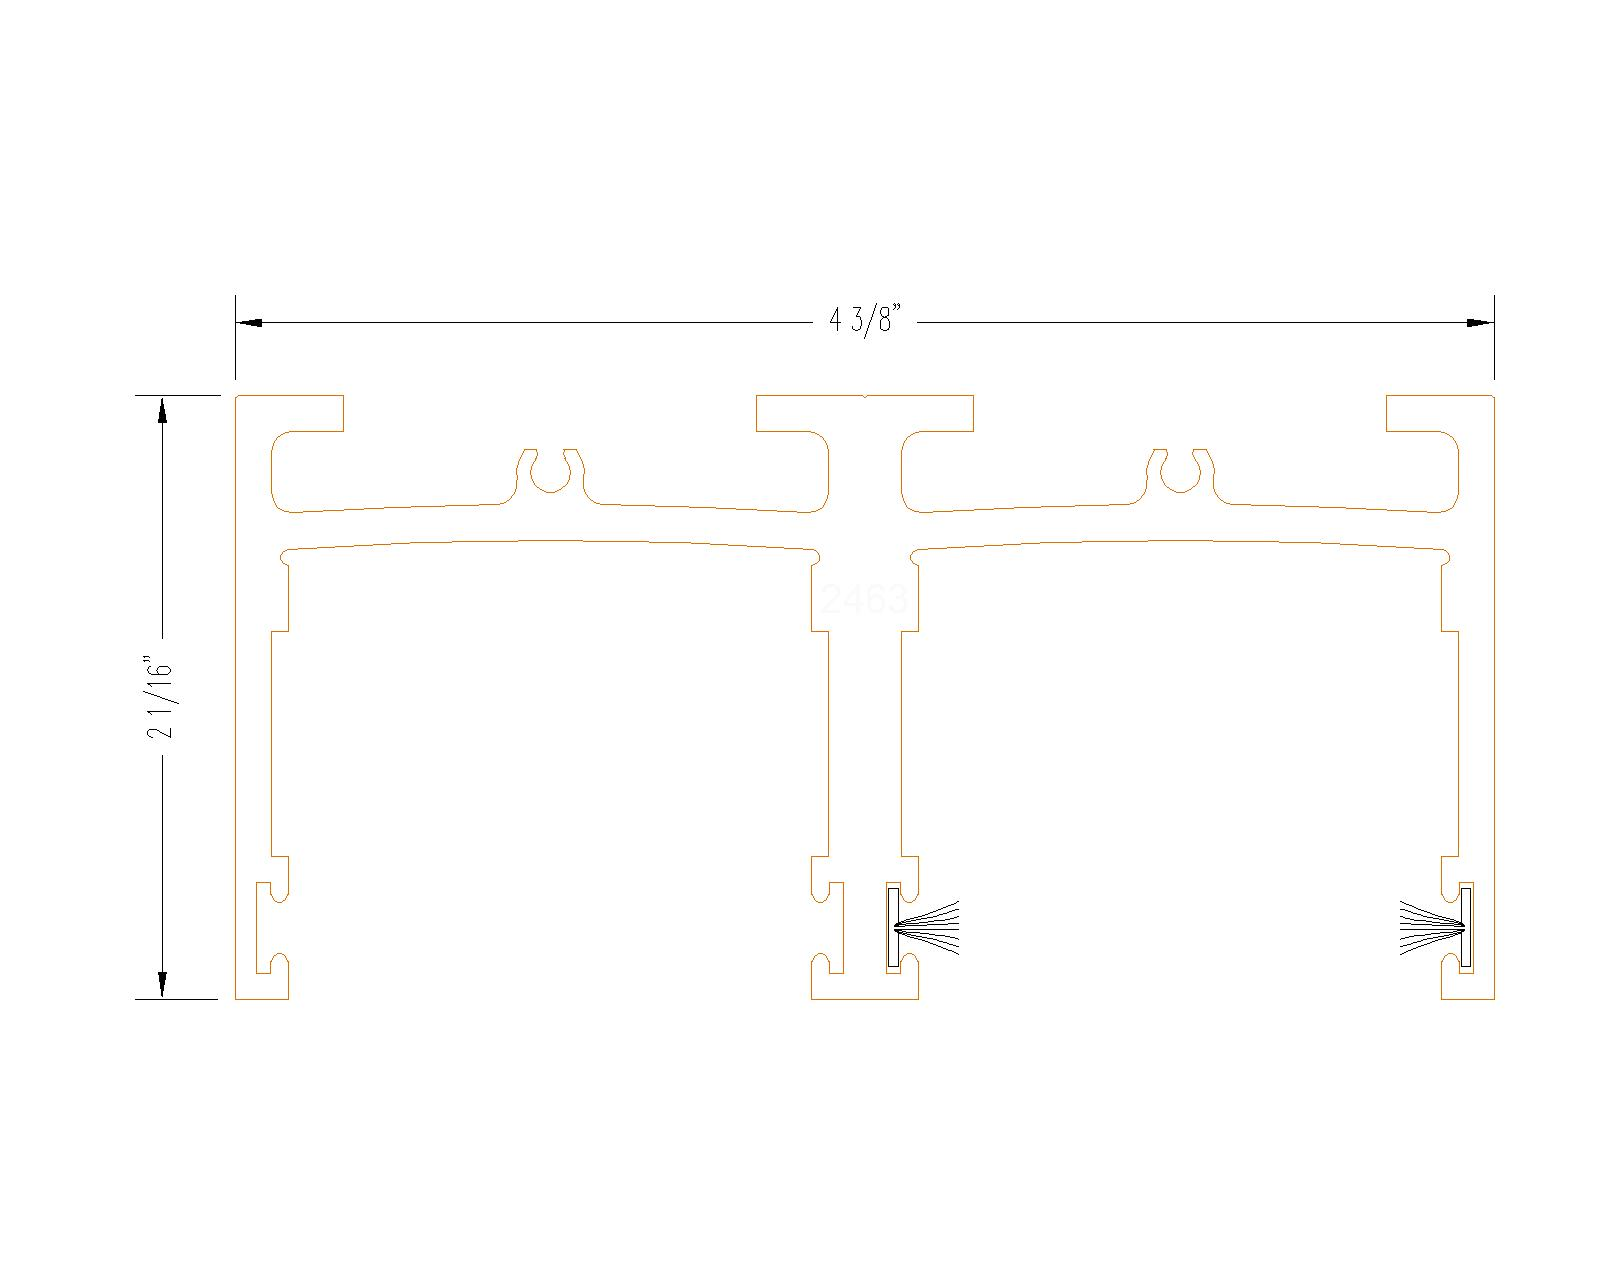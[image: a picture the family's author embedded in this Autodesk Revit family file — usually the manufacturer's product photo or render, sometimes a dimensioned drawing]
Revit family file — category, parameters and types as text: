
# Revit family: PRLMaxSlider_WallSystem
name_source: partatom
category: Puertas
units: mm (PartAtom-declared; Revit-internal decimal feet)

## family parameters
Anfitrión = Muro
Compartido = No
Corte con vacíos al cargar = No
Número OmniClass = 23.30.10.00
Punto de cálculo de habitación = No
Siempre vertical = Sí
Título OmniClass = Doors

## types (1)
- PRLMaxSlider_WallSystem
    Altura = 7' - 0"
    Altura aproximada = 7' - 0"
    Anchura = 10' - 0"
    Anchura aproximada = 10' - 0"
    Cierre de muro = Por anfitrión
    Configurations = PRL Wall System
    Fabricante = PRL
    Frame Projection Ext. = 0' - 1"
    Frame Projection Int. = 0' - 1"
    Frame Width = 0' - 3"
    Glass_Thickness = 1/2"
    H_TopRail_B = 6' - 10 11/32"
    Height = 7' - 0"
    MF2 = PRL MS
    Modelo = Max Slider Wall System
    Number Fixed Panels = 1
    Roller Options = PRL Cancun Series (Bottom Roller)
    TH_SingleFrame = 0' - 2 3/16"
    URL = https://www.prlglass.com
    Width = 10' - 0"
    X01G = 1 1/8"
    X01W = PRL Wall System
    X02G = 1/2"
    X02M = PRL Wall System
    X03G = 1/4"
    X03P = PRL Wall System
    X04B = PRL Wall System
    XCON = PRL Wall System
    XConfig = WallSystem XO (Left) : WallSystem
    XR0 = PRL Cabo Series (Top Hung)
    XR1 = PRL Cancun Series (Bottom Roller)
    XRCON = PRL Cancun Series (Bottom Roller)
    XWSL = WallSystem XO (Left) : WallSystem
    XWSR = WallSystem OX (Right)

## geometry (parser evidence)
native form markers: Sweep x65
no freeform markers — native parametric forms only
